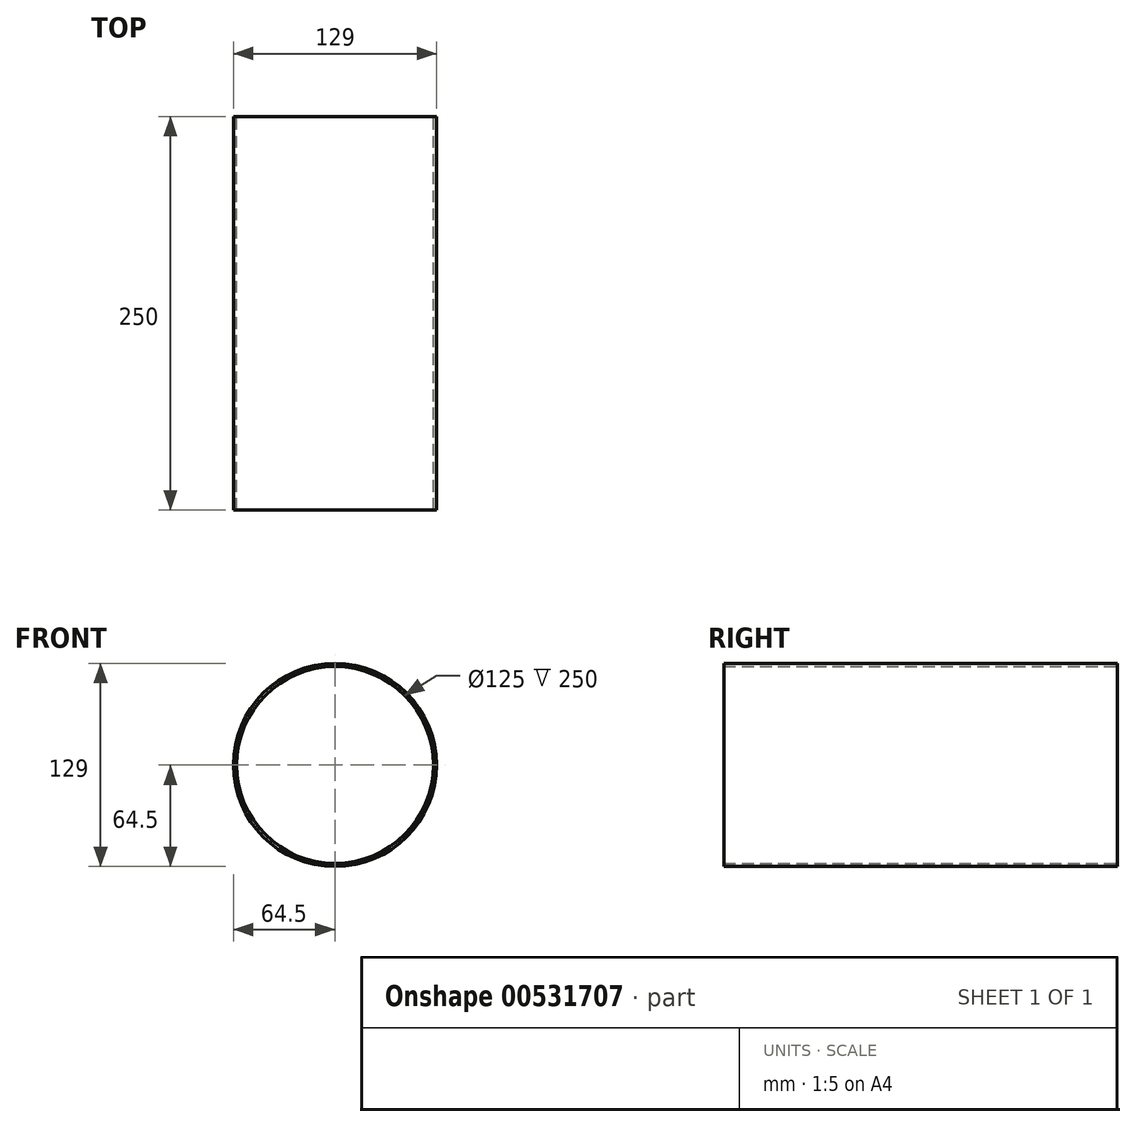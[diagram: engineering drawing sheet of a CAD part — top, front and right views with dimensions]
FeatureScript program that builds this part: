
annotation { "Feature Type Name" : "Feature", "Feature Type Description" : "" }
export const myFeature = defineFeature(function(context is Context, id is Id, definition is map)
    precondition{}
    {
        {
            var Q0;
            Q0=qCreatedBy(makeId("Front.planeOp"),FACE);
            var sketch = newSketch(context, id + "F0", { "sketchPlane" : qUnion([Q0])});
            skCircle(sketch, "E0", {"center": v(0, 0) * mm, "radius": 62.5 * mm});
            skCircle(sketch, "E1", {"center": v(0, 0) * mm, "radius": 64.5 * mm});
            skSolve(sketch);
        }
        {
            var Q0;
            Q0=makeQuery(id+"F0.imprint","IMPRINT",FACE,{"disambiguationData":[TD([[makeQuery(id+"F0.imprint","IMPRINT",EDGE,{"derivedFrom":sQuery(id+"F0.wireOp",EDGE,"E0")}),-1.0]])]});
            extrude(context, id + "F1", {"entities" : qUnion([Q0]), "endBound" : BoundingType.SYMMETRIC, "depth" : (310 - 60) * mm, "offsetDistance" : 25 * mm});
        }
    });
